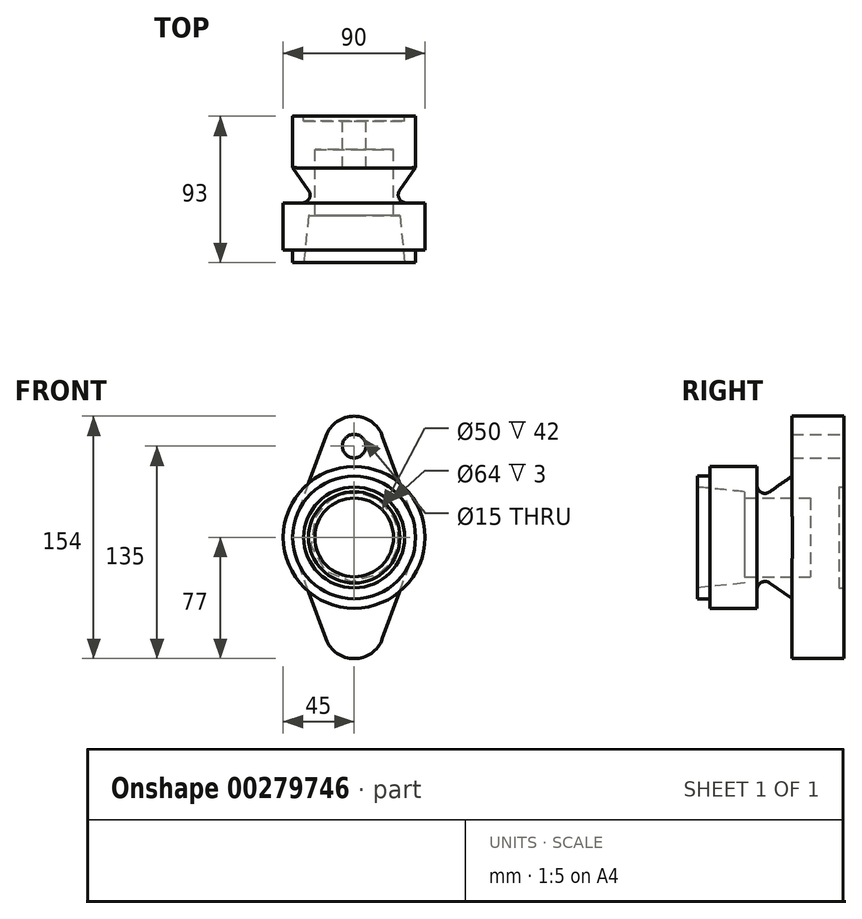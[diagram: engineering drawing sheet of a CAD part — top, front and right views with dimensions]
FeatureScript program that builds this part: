
annotation { "Feature Type Name" : "Feature", "Feature Type Description" : "" }
export const myFeature = defineFeature(function(context is Context, id is Id, definition is map)
    precondition{}
    {
        {
            var Q0;
            Q0=qCreatedBy(makeId("Right.planeOp"),FACE);
            var sketch = newSketch(context, id + "F0", { "sketchPlane" : qUnion([Q0])});
            skLineSegment(sketch, "E0", {"start": v(-21.52, 39) * mm, "end": v(-13.52, 39) * mm});
            skLineSegment(sketch, "E1", {"start": v(-13.52, 39) * mm, "end": v(-13.52, 45) * mm});
            skLineSegment(sketch, "E2", {"start": v(-13.52, 45) * mm, "end": v(16.48, 45) * mm});
            skLineSegment(sketch, "E3", {"start": v(16.48, 45) * mm, "end": v(16.48, 32.98) * mm});
            skLineSegment(sketch, "E4", {"start": v(71.48, 39) * mm, "end": v(71.48, 32) * mm});
            skLineSegment(sketch, "E5", {"start": v(71.48, 32) * mm, "end": v(68.48, 32) * mm});
            skLineSegment(sketch, "E6", {"start": v(68.48, 32) * mm, "end": v(68.48, 0) * mm});
            skLineSegment(sketch, "E7", {"start": v(68.48, 0) * mm, "end": v(50.48, 0) * mm});
            skLineSegment(sketch, "E8", {"start": v(50.48, 0) * mm, "end": v(50.48, 25) * mm});
            skLineSegment(sketch, "E9", {"start": v(50.48, 25) * mm, "end": v(8.48, 25) * mm});
            skLineSegment(sketch, "E10", {"start": v(8.48, 25) * mm, "end": v(8.48, 29) * mm});
            skLineSegment(sketch, "E11", {"start": v(-21.52, 32) * mm, "end": v(-21.52, 39) * mm});
            skPoint(sketch, "E12.end.orphan", {"position": v(39.6, 45) * mm});
            skLineSegment(sketch, "E13", {"start": v(71.48, 39) * mm, "end": v(38.8, 39) * mm});
            skLineSegment(sketch, "E14", {"start": v(38.8, 39) * mm, "end": v(24.35, 28.88) * mm});
            skPoint(sketch, "E15.visualSharp", {"position": v(16.48, 23.38) * mm});
            skArc(sketch, "E15.filletArc", {"start": v(16.48, 32.98) * mm, "mid": v(19.17, 28.54) * mm, "end": v(24.35, 28.88) * mm});
            skLineSegment(sketch, "E16", {"start": v(-21.52, 32) * mm, "end": v(8.48, 29) * mm});
            skPoint(sketch, "E17.orphan", {"position": v(8.48, 33) * mm});
            skSolve(sketch);
        }
        {
            var Q0;
            Q0=makeQuery(id+"F0.imprint","IMPRINT",FACE,{"disambiguationData":[TD([[makeQuery(id+"F0.imprint","IMPRINT",EDGE,{"derivedFrom":sQuery(id+"F0.wireOp",EDGE,"E0")}),-1.0]])]});
            var Q1;
            Q1=sQuery(id+"F0.wireOp",EDGE,"E7");
            revolve(context, id + "F1", {"entities" : qUnion([Q0]), "axis" : qUnion([Q1]), "revolveType" : RevolveType.FULL});
        }
        {
            var Q0;
            Q0=makeQuery(id+"F1.opRevolve","SWEPT_FACE",FACE,{"disambiguationData":[OSD([sQuery(id+"F0.wireOp",EDGE,"E4")])]});
            var sketch = newSketch(context, id + "F2", { "sketchPlane" : qUnion([Q0])});
            skLineSegment(sketch, "E18", {"start": v(0, 0) * mm, "end": v(0, 58) * mm, "construction": true});
            skLineSegment(sketch, "E19", {"start": v(13.9, 58) * mm, "end": v(-13.9, 58) * mm, "construction": true});
            skCircle(sketch, "E20", {"center": v(0, 58) * mm, "radius": 7.5 * mm});
            skLineSegment(sketch, "E21", {"start": v(0, 39) * mm, "end": v(0, 39) * mm});
            skLineSegment(sketch, "E22", {"start": v(-17.83, 64.55) * mm, "end": v(-36.6, 13.45) * mm});
            skLineSegment(sketch, "E23", {"start": v(17.83, 64.55) * mm, "end": v(36.6, 13.45) * mm});
            skArc(sketch, "E24", {"start": v(36.6, -13.45) * mm, "mid": v(39, 0) * mm, "end": v(36.6, 13.45) * mm});
            skArc(sketch, "E25.MirrorC", {"start": v(-17.83, 64.55) * mm, "mid": v(0, 77) * mm, "end": v(17.83, 64.55) * mm});
            skLineSegment(sketch, "E26.MirrorCS", {"start": v(17.83, -64.55) * mm, "end": v(36.6, -13.45) * mm});
            skLineSegment(sketch, "E27.MirrorC", {"start": v(0, -39) * mm, "end": v(0, -39) * mm});
            skCircle(sketch, "E28.MirrorC", {"center": v(0, -58) * mm, "radius": 7.5 * mm});
            skLineSegment(sketch, "E29.MirrorCS", {"start": v(-17.83, -64.55) * mm, "end": v(-36.6, -13.45) * mm});
            skArc(sketch, "E30", {"start": v(-36.6, -13.45) * mm, "mid": v(0, -39) * mm, "end": v(36.6, -13.45) * mm});
            skArc(sketch, "E31.trimOffspring", {"start": v(17.83, -64.55) * mm, "mid": v(0, -77) * mm, "end": v(-17.83, -64.55) * mm});
            skArc(sketch, "E32.trimOffspring", {"start": v(-36.6, 13.45) * mm, "mid": v(-39, 0) * mm, "end": v(-36.6, -13.45) * mm});
            skArc(sketch, "E33.trimOffspring", {"start": v(17.83, 64.55) * mm, "mid": v(0, 77) * mm, "end": v(-17.83, 64.55) * mm});
            skArc(sketch, "E34.trimOffspring", {"start": v(36.6, 13.45) * mm, "mid": v(0, 39) * mm, "end": v(-36.6, 13.45) * mm});
            skSolve(sketch);
        }
        {
            var Q0;
            Q0=makeQuery(id+"F2.imprint","IMPRINT",FACE,{"disambiguationData":[TD([[makeQuery(id+"F2.imprint","IMPRINT",EDGE,{"derivedFrom":sQuery(id+"F2.wireOp",EDGE,"E20")}),1.0]])]});
            var Q1;
            Q1=makeQuery(id+"F2.imprint","IMPRINT",FACE,{"disambiguationData":[TD([[makeQuery(id+"F2.imprint","IMPRINT",EDGE,{"derivedFrom":sQuery(id+"F2.wireOp",EDGE,"E28.MirrorC")}),1.0]])]});
            extrude(context, id + "F3", {"entities" : qUnion([Q0, Q1]), "operationType" : NewBodyOperationType.ADD, "oppositeDirection" : true, "depth" : 33 * mm});
        }
        {
            var Q0;
            Q0=makeQuery(id+"F2.imprint","IMPRINT",FACE,{"disambiguationData":[TD([[makeQuery(id+"F2.imprint","IMPRINT",EDGE,{"derivedFrom":sQuery(id+"F2.wireOp",EDGE,"E26.MirrorCS")}),1.0]])]});
            var Q1;
            Q1=makeQuery(id+"F2.imprint","IMPRINT",FACE,{"disambiguationData":[TD([[makeQuery(id+"F2.imprint","IMPRINT",EDGE,{"derivedFrom":sQuery(id+"F2.wireOp",EDGE,"E22")}),1.0]])]});
            extrude(context, id + "F4", {"entities" : qUnion([Q0, Q1]), "operationType" : NewBodyOperationType.ADD, "oppositeDirection" : true, "depth" : 33 * mm});
        }
    });
